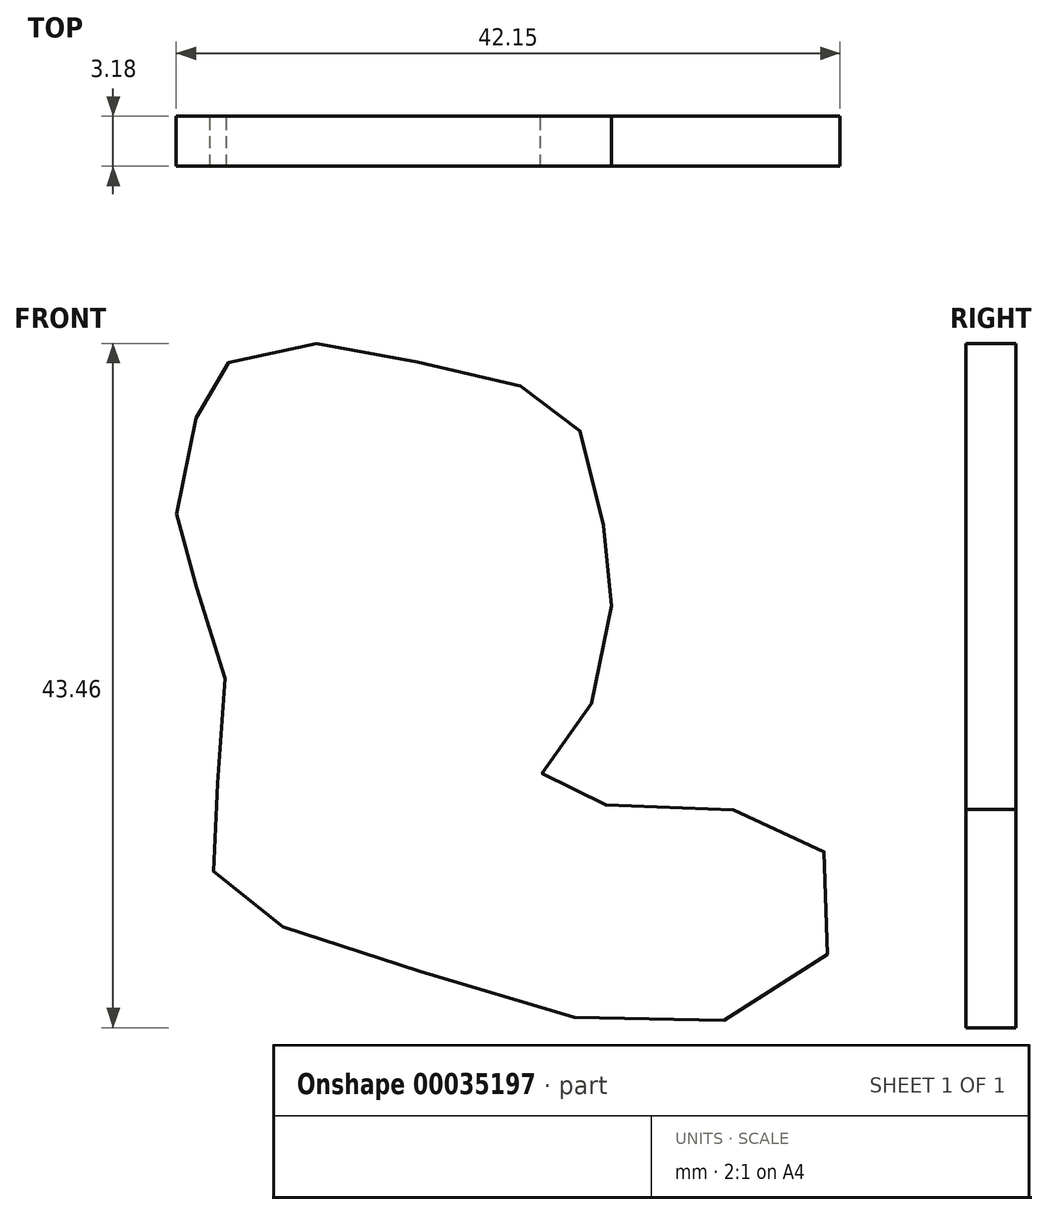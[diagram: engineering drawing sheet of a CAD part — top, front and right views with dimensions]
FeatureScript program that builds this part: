
annotation { "Feature Type Name" : "Feature", "Feature Type Description" : "" }
export const myFeature = defineFeature(function(context is Context, id is Id, definition is map)
    precondition{}
    {
        {
            var Q0;
            Q0=qCreatedBy(makeId("Front.planeOp"),FACE);
            var sketch = newSketch(context, id + "F0", { "sketchPlane" : qUnion([Q0])});
            skFitSpline(sketch, "E0", {"points": [v(-30.5, 17.89) * mm, v(-29.26, 20.8) * mm, v(-24.27, 22.6) * mm, v(-16.64, 21.5) * mm, v(-8.87, 19.55) * mm, v(-5.96, 16.78) * mm, v(-4.44, 9.7) * mm, v(-4.16, 5.13) * mm, v(-6.52, -2.36) * mm, v(-8.6, -5.13) * mm, v(-1.8, -6.93) * mm, v(8.04, -8.18) * mm, v(9.98, -15.4) * mm, v(0, -20.8) * mm, v(-18.17, -16.64) * mm, v(-28.57, -12.34) * mm, v(-29.54, -7.9) * mm, v(-28.57, 0) * mm, v(-30.37, 6.93) * mm, v(-31.75, 10.95) * mm, v(-30.5, 17.89) * mm]});
            skSolve(sketch);
        }
        {
            var Q0;
            Q0=makeQuery(id+"F0.imprint","IMPRINT",FACE,{"disambiguationData":[TD([[makeQuery(id+"F0.imprint","IMPRINT",EDGE,{"derivedFrom":sQuery(id+"F0.wireOp",EDGE,"E0")}),-1.0]])]});
            extrude(context, id + "F1", {"entities" : qUnion([Q0]), "depth" : 3.17 * mm});
        }
    });
